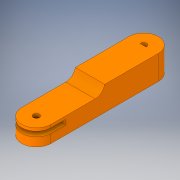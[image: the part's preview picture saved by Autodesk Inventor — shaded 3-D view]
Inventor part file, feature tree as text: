
AUTODESK INVENTOR PART (.ipt)
format: ipt  version: 2017 (Build 210142000, 142)  size: 157,696 bytes
history: native  units: in
note: dims shown in document units (in); Inventor stores cm internally (conversion verified against a paired STEP export)
features: extrude x3, sketch x2, fillet x1
ambient origin geometry x8: Origin, YZ Plane, XZ Plane, XY Plane, X Axis, Y Axis, Z Axis, Center Point
bodies: Solid1 (feature_tree)
feature tree (6):
  extrude  "Extrusion1"  Depth=0.75in
  extrude  "Extrusion3"  TaperAngle=0.0deg  [1 undecoded]
  fillet  "Fillet3"  Radius=0.25in
  extrude  "Extrusion4"  Depth=0.3937in TaperAngle=0.0deg
  sketch  "Sketch1"  dims[d0=1.5in d2=0.75in]
  sketch  "Sketch4"  dims[d3=0.3125in d6=0.0in d15=0.25in d17=0.3937in d18=0.0in d19=0.45in d20=0.4in d21=3.5in d22=0.5in d23=0.25in d24=1.0in d25=0.0in]
note: 1 required parameter value undecoded (feature->parameter linkage not recoverable at this tier; creation-order binding heuristic only, values carry confidence <= 0.55)
